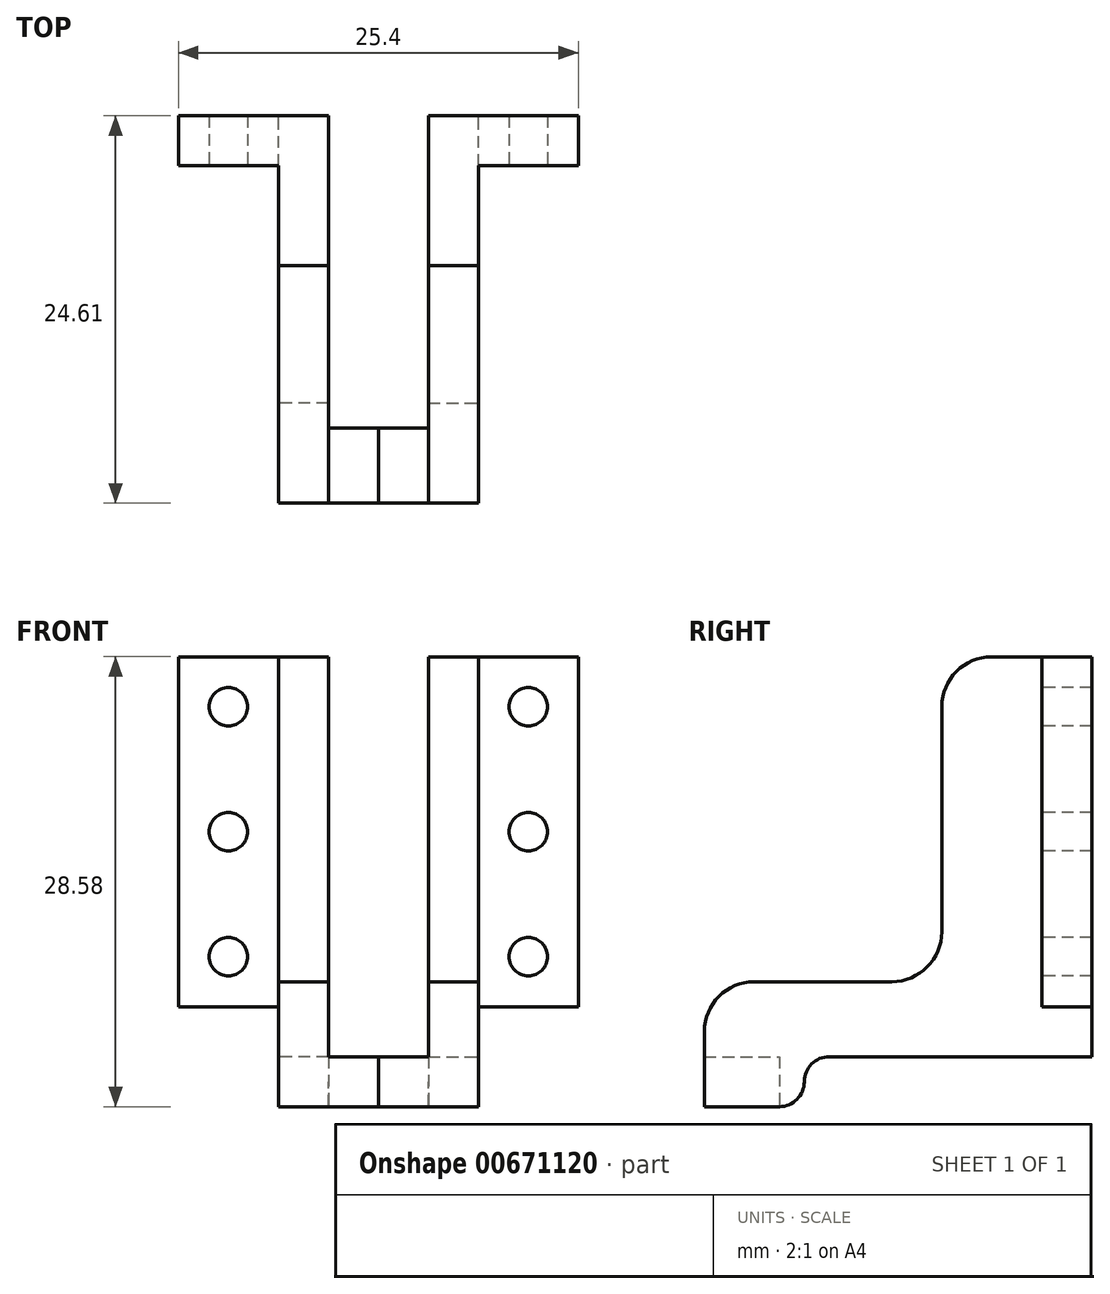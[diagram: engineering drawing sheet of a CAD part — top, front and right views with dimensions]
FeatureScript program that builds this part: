
annotation { "Feature Type Name" : "Feature", "Feature Type Description" : "" }
export const myFeature = defineFeature(function(context is Context, id is Id, definition is map)
    precondition{}
    {
        {
            var Q0;
            Q0=qCreatedBy(makeId("Right.planeOp"),FACE);
            var sketch = newSketch(context, id + "F0", { "sketchPlane" : qUnion([Q0])});
            skLineSegment(sketch, "E0", {"start": v(31.33, 44.33) * mm, "end": v(37.68, 44.33) * mm});
            skLineSegment(sketch, "E1", {"start": v(37.68, 44.33) * mm, "end": v(37.68, 18.93) * mm});
            skLineSegment(sketch, "E2", {"start": v(37.68, 18.93) * mm, "end": v(21, 18.93) * mm});
            skLineSegment(sketch, "E3", {"start": v(19.42, 17.34) * mm, "end": v(19.42, 17.34) * mm});
            skLineSegment(sketch, "E4", {"start": v(17.83, 15.75) * mm, "end": v(13.07, 15.75) * mm});
            skLineSegment(sketch, "E5", {"start": v(13.07, 15.75) * mm, "end": v(13.07, 20.51) * mm});
            skLineSegment(sketch, "E6", {"start": v(16.24, 23.69) * mm, "end": v(24.98, 23.69) * mm});
            skLineSegment(sketch, "E7", {"start": v(28.15, 26.86) * mm, "end": v(28.15, 41.15) * mm});
            skPoint(sketch, "E8.orphan", {"position": v(13.07, 15.75) * mm});
            skPoint(sketch, "E9.orphan", {"position": v(13.07, 22.67) * mm});
            skPoint(sketch, "E10.visualSharp", {"position": v(28.15, 44.33) * mm});
            skArc(sketch, "E10.filletArc", {"start": v(31.33, 44.33) * mm, "mid": v(29.08, 43.4) * mm, "end": v(28.15, 41.15) * mm});
            skPoint(sketch, "E11.visualSharp", {"position": v(28.15, 23.69) * mm});
            skArc(sketch, "E11.filletArc", {"start": v(24.98, 23.69) * mm, "mid": v(27.22, 24.62) * mm, "end": v(28.15, 26.86) * mm});
            skPoint(sketch, "E12.visualSharp", {"position": v(13.07, 23.69) * mm});
            skArc(sketch, "E12.filletArc", {"start": v(16.24, 23.69) * mm, "mid": v(14, 22.76) * mm, "end": v(13.07, 20.51) * mm});
            skPoint(sketch, "E13.visualSharp", {"position": v(19.42, 18.93) * mm});
            skArc(sketch, "E13.filletArc", {"start": v(21, 18.93) * mm, "mid": v(19.88, 18.46) * mm, "end": v(19.42, 17.34) * mm});
            skPoint(sketch, "E14.visualSharp", {"position": v(19.42, 15.75) * mm});
            skArc(sketch, "E14.filletArc", {"start": v(17.83, 15.75) * mm, "mid": v(18.95, 16.22) * mm, "end": v(19.42, 17.34) * mm});
            skSolve(sketch);
        }
        {
            var Q0;
            Q0=qSketchRegion(id+"F0",true);
            extrude(context, id + "F1", {"entities" : qUnion([Q0]), "depth" : 3.17 * mm});
        }
        {
            var Q0;
            Q0=makeQuery(id+"F1.opExtrude","CAP_FACE",FACE,{"disambiguationData":[OSD([sQuery(id+"F0.wireOp",EDGE,"E0"),sQuery(id+"F0.wireOp",EDGE,"E1"),sQuery(id+"F0.wireOp",EDGE,"E2"),sQuery(id+"F0.wireOp",EDGE,"E4"),sQuery(id+"F0.wireOp",EDGE,"E5"),sQuery(id+"F0.wireOp",EDGE,"E6"),sQuery(id+"F0.wireOp",EDGE,"E7"),sQuery(id+"F0.wireOp",EDGE,"E10.filletArc"),sQuery(id+"F0.wireOp",EDGE,"E11.filletArc"),sQuery(id+"F0.wireOp",EDGE,"E12.filletArc"),sQuery(id+"F0.wireOp",EDGE,"E13.filletArc"),sQuery(id+"F0.wireOp",EDGE,"E14.filletArc")])],"isStart":false});
            var sketch = newSketch(context, id + "F2", { "sketchPlane" : qUnion([Q0])});
            skLineSegment(sketch, "E15", {"start": v(13.07, 18.93) * mm, "end": v(17.83, 18.93) * mm});
            skLineSegment(sketch, "E16", {"start": v(17.83, 18.93) * mm, "end": v(17.83, 15.75) * mm});
            skSolve(sketch);
        }
        {
            var Q0;
            Q0=qSketchRegion(id+"F2",true);
            var Q1;
            {var subQ0=sQuery(id+"F2.wireOp",EDGE,"E15");Q1=makeQuery(id+"F2.imprint","IMPRINT",FACE,{"disambiguationData":[TD([[makeQuery(id+"F2.imprint","IMPRINT",EDGE,{"derivedFrom":subQ0}),-1.0]])]});}
            extrude(context, id + "F3", {"entities" : qUnion([Q0, Q1]), "operationType" : NewBodyOperationType.ADD, "depth" : 3.17 * mm});
        }
        {
            var Q0;
            Q0=makeQuery(id+"F1.opExtrude","CAP_FACE",FACE,{"disambiguationData":[OSD([sQuery(id+"F0.wireOp",EDGE,"E0"),sQuery(id+"F0.wireOp",EDGE,"E1"),sQuery(id+"F0.wireOp",EDGE,"E2"),sQuery(id+"F0.wireOp",EDGE,"E4"),sQuery(id+"F0.wireOp",EDGE,"E5"),sQuery(id+"F0.wireOp",EDGE,"E6"),sQuery(id+"F0.wireOp",EDGE,"E7"),sQuery(id+"F0.wireOp",EDGE,"E10.filletArc"),sQuery(id+"F0.wireOp",EDGE,"E11.filletArc"),sQuery(id+"F0.wireOp",EDGE,"E12.filletArc"),sQuery(id+"F0.wireOp",EDGE,"E13.filletArc"),sQuery(id+"F0.wireOp",EDGE,"E14.filletArc")])],"isStart":true});
            var sketch = newSketch(context, id + "F4", { "sketchPlane" : qUnion([Q0])});
            skLineSegment(sketch, "E17", {"start": v(-34.5, 44.33) * mm, "end": v(-34.5, 22.1) * mm});
            skLineSegment(sketch, "E18", {"start": v(-34.5, 22.1) * mm, "end": v(-37.68, 22.1) * mm});
            skSolve(sketch);
        }
        {
            var Q0;
            {var subQ0=sQuery(id+"F4.wireOp",EDGE,"E17");Q0=makeQuery(id+"F4.imprint","IMPRINT",FACE,{"disambiguationData":[TD([[makeQuery(id+"F4.imprint","IMPRINT",EDGE,{"derivedFrom":subQ0}),-1.0]])]});}
            extrude(context, id + "F5", {"entities" : qUnion([Q0]), "operationType" : NewBodyOperationType.ADD, "depth" : 6.35 * mm});
        }
        {
            var Q0;
            Q0=makeQuery(id+"F5.opExtrude","SWEPT_FACE",FACE,{"disambiguationData":[OSD([sQuery(id+"F4.wireOp",EDGE,"E17")])]});
            var sketch = newSketch(context, id + "F6", { "sketchPlane" : qUnion([Q0])});
            skCircle(sketch, "E19", {"center": v(-3.18, 41.15) * mm, "radius": 1.22 * mm});
            skCircle(sketch, "E20", {"center": v(-3.18, 33.21) * mm, "radius": 1.22 * mm});
            skCircle(sketch, "E21", {"center": v(-3.18, 25.28) * mm, "radius": 1.22 * mm});
            skSolve(sketch);
        }
        {
            var Q0;
            Q0=makeQuery(id+"F6.imprint","IMPRINT",FACE,{"disambiguationData":[TD([[makeQuery(id+"F6.imprint","IMPRINT",EDGE,{"derivedFrom":sQuery(id+"F6.wireOp",EDGE,"E19")}),1.0]])]});
            var Q1;
            Q1=makeQuery(id+"F6.imprint","IMPRINT",FACE,{"disambiguationData":[TD([[makeQuery(id+"F6.imprint","IMPRINT",EDGE,{"derivedFrom":sQuery(id+"F6.wireOp",EDGE,"E20")}),1.0]])]});
            var Q2;
            Q2=makeQuery(id+"F6.imprint","IMPRINT",FACE,{"disambiguationData":[TD([[makeQuery(id+"F6.imprint","IMPRINT",EDGE,{"derivedFrom":sQuery(id+"F6.wireOp",EDGE,"E21")}),1.0]])]});
            extrude(context, id + "F7", {"entities" : qUnion([Q0, Q1, Q2]), "operationType" : NewBodyOperationType.REMOVE, "oppositeDirection" : true, "depth" : 25.4 * mm});
        }
        {
            var Q0;
            Q0=makeQuery(id+"F1.opExtrude","SWEPT_BODY",BODY,{"disambiguationData":[OSD([sQuery(id+"F0.wireOp",EDGE,"E0"),sQuery(id+"F0.wireOp",EDGE,"E1"),sQuery(id+"F0.wireOp",EDGE,"E2"),sQuery(id+"F0.wireOp",EDGE,"E4"),sQuery(id+"F0.wireOp",EDGE,"E5"),sQuery(id+"F0.wireOp",EDGE,"E6"),sQuery(id+"F0.wireOp",EDGE,"E7"),sQuery(id+"F0.wireOp",EDGE,"E10.filletArc"),sQuery(id+"F0.wireOp",EDGE,"E11.filletArc"),sQuery(id+"F0.wireOp",EDGE,"E12.filletArc"),sQuery(id+"F0.wireOp",EDGE,"E13.filletArc"),sQuery(id+"F0.wireOp",EDGE,"E14.filletArc")])]});
            var Q1;
            Q1=makeQuery(id+"F3.opExtrude","CAP_FACE",FACE,{"disambiguationData":[OSD([sQuery(id+"F0.wireOp",EDGE,"E4"),sQuery(id+"F0.wireOp",EDGE,"E5"),sQuery(id+"F2.wireOp",EDGE,"E15"),sQuery(id+"F2.wireOp",EDGE,"E16")])],"isStart":false});
            mirror(context, id + "F8", {"entities" : qUnion([Q0]), "mirrorPlane" : qUnion([Q1])});
        }
    });
